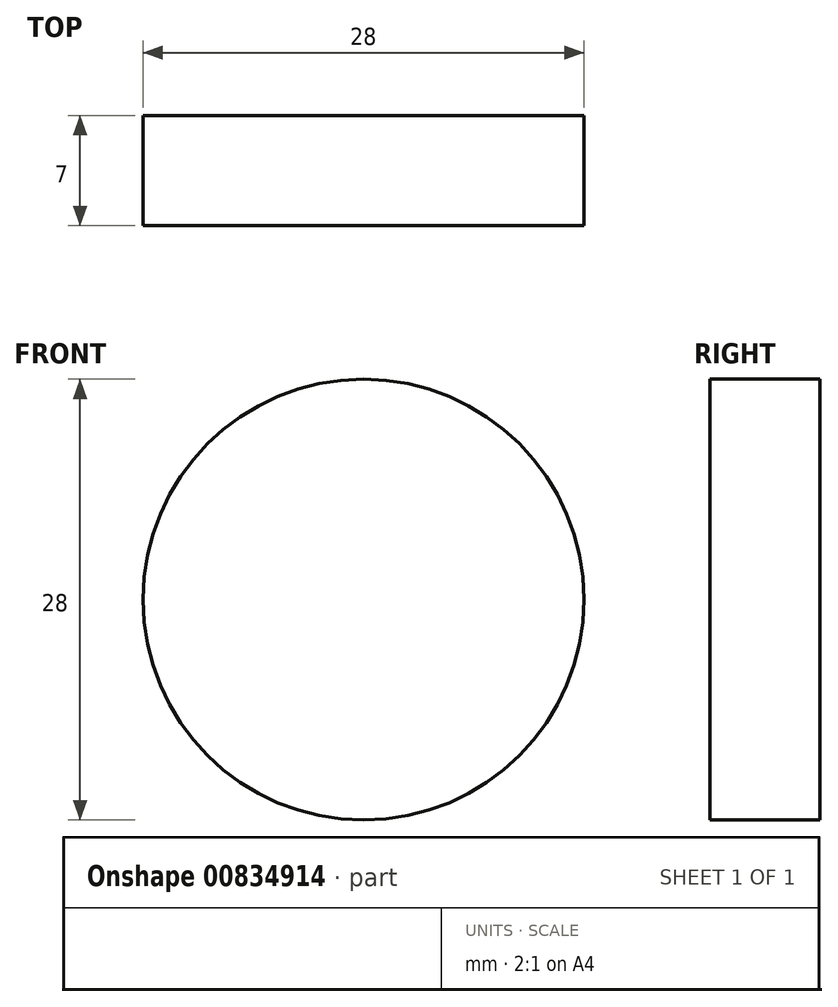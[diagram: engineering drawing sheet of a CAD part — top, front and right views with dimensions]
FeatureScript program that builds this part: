
annotation { "Feature Type Name" : "Feature", "Feature Type Description" : "" }
export const myFeature = defineFeature(function(context is Context, id is Id, definition is map)
    precondition{}
    {
        {
            var Q0;
            Q0=qCreatedBy(makeId("Front.planeOp"),FACE);
            var sketch = newSketch(context, id + "F0", { "sketchPlane" : qUnion([Q0])});
            skCircle(sketch, "E0", {"center": v(0, 0) * mm, "radius": 14 * mm});
            skSolve(sketch);
        }
        {
            var Q0;
            Q0=makeQuery(id+"F0.imprint","IMPRINT",FACE,{"disambiguationData":[TD([[makeQuery(id+"F0.imprint","IMPRINT",EDGE,{"derivedFrom":sQuery(id+"F0.wireOp",EDGE,"E0")}),1.0]])]});
            extrude(context, id + "F1", {"entities" : qUnion([Q0]), "depth" : 7 * mm, "offsetDistance" : 25 * mm});
        }
    });
